# Revit family: Tub_Spout-DXV-Modulus-D35120760_Series
name_source: partatom
category: Plumbing Fixtures
units: mm (PartAtom-declared; Revit-internal decimal feet)

## family parameters
Cut with Voids When Loaded = No
Host = Face
OmniClass Number = 23.45.05.14.21
OmniClass Title = Bathtubs
Part Type = Normal
Room Calculation Point = No
Round Connector Dimension = Use Diameter
Shared = Yes

## types (4) — shared parameters
1/2" Connection Option = Yes
3/4" Connection Option = No
ASME A112.18.1/CSA B125.1 = Yes
Assembly Code = D2020300
CW Connection = Yes
CWFU = 3
Default Elevation = 21"
Description = DXV Modulus Wall Tub Spout
HW Connection = Yes
HWFU = 3
Height = 2 9/16"
Inlet Connection Description = 1/2'' Water Connection
Inlet Diameter Connection = 1/2"
Installation Instruction Link = https://dxv01.blob.core.windows.net
Installation Type = Wall Mounted
Length = 9 5/8"
Manufacturer = DXV
Price = Prices may vary. Please consult Manufacturer Representative for most up-to-date price list.
Product Documentation Link = https://dxv01.blob.core.windows.net
Product Page URL = https://www.dxv.com
Revised Date = 04/06/2022
URL = https://www.dxv.com
Vent Connection = No
WFU = 4
Waste Connection = No
Width = 2"

## per-type parameters (varying)
| type | Finish | Finish 2 | Material |
| D35120760.100 | Brass-DXV-100-Polished Chrome | Brass-DXV-144-Brushed Nickel | Brass-DXV-100-Polished Chrome |
| D35120760.144 | Brass-DXV-144-Brushed Nickel | Brass-DXV-100-Polished Chrome | Brass-DXV-144-Brushed Nickel |
| D35120760.150 | Brass-DXV-150-Platinum Nickel | Brass-DXV-144-Brushed Nickel | Brass-DXV-150-Platinum Nickel |
| D35120760.243 | Brass-DXV-243-Matte Black | Brass-DXV-243-Matte Black | Brass-DXV-243-Matte Black |

note: column(s) folded — value = type name in every type: Model

## geometry (parser evidence)
native form markers: Sweep x3
no freeform markers — native parametric forms only
